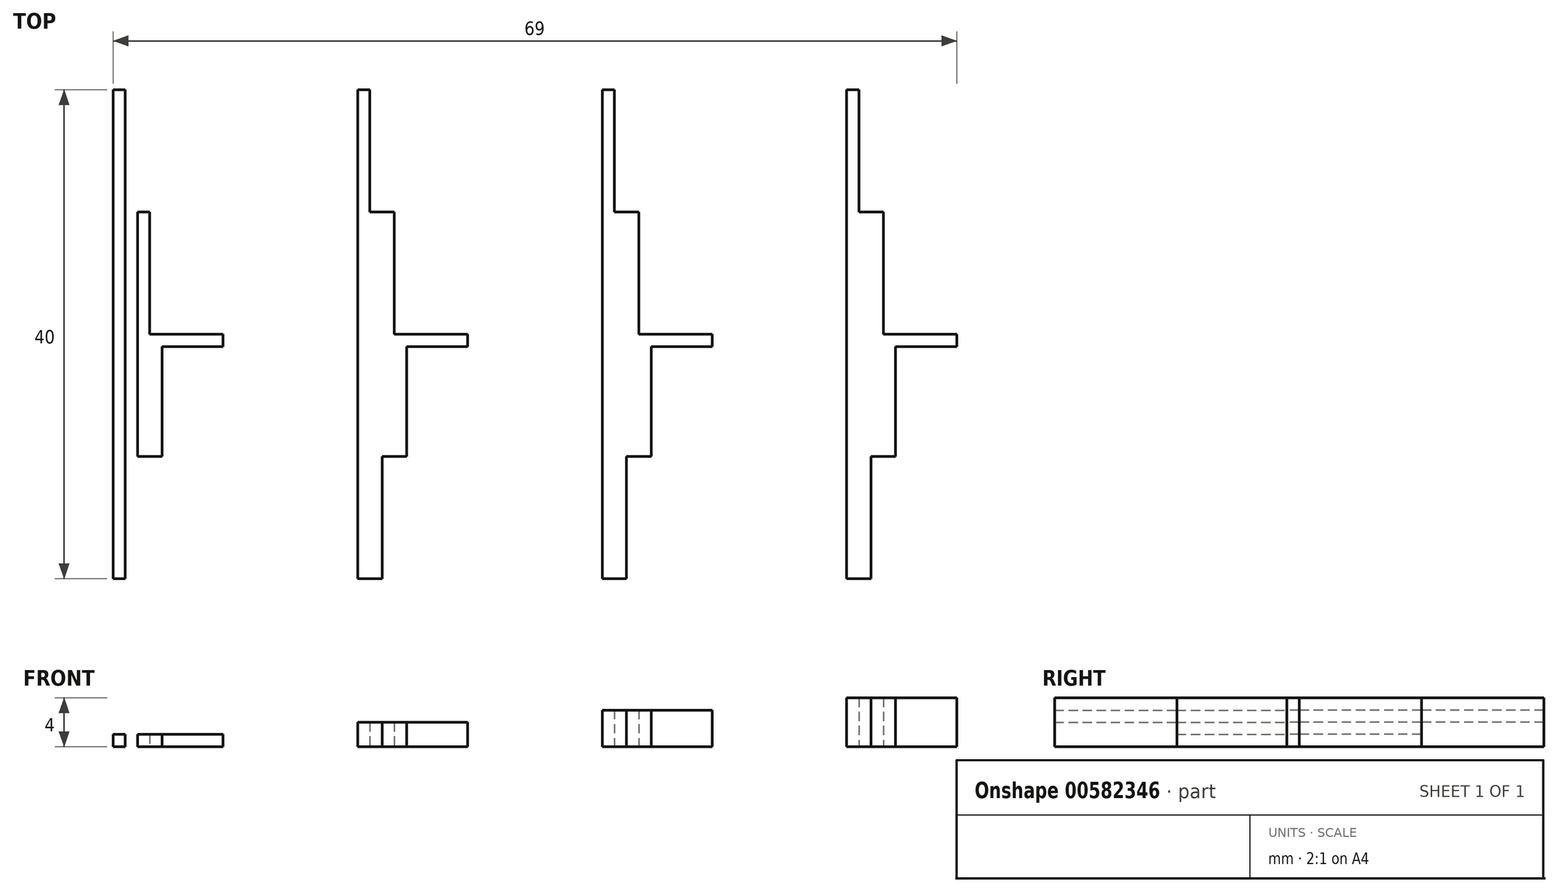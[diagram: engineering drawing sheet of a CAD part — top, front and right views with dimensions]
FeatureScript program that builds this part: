
annotation { "Feature Type Name" : "Feature", "Feature Type Description" : "" }
export const myFeature = defineFeature(function(context is Context, id is Id, definition is map)
    precondition{}
    {
        {
            var Q0;
            Q0=qCreatedBy(makeId("Top.planeOp"),FACE);
            var sketch = newSketch(context, id + "F0", { "sketchPlane" : qUnion([Q0])});
            skLineSegment(sketch, "E0.bottom", {"start": v(-46.97, 24.85) * mm, "end": v(-45.97, 24.85) * mm});
            skLineSegment(sketch, "E0.top", {"start": v(-46.97, -15.15) * mm, "end": v(-45.97, -15.15) * mm});
            skLineSegment(sketch, "E0.left", {"start": v(-46.97, 24.85) * mm, "end": v(-46.97, -15.15) * mm});
            skLineSegment(sketch, "E0.right", {"start": v(-45.97, 24.85) * mm, "end": v(-45.97, -15.15) * mm});
            skLineSegment(sketch, "E1.bottom", {"start": v(-46.97, -15.15) * mm, "end": v(-44.97, -15.15) * mm});
            skLineSegment(sketch, "E2.bottom", {"start": v(-44.97, -15.15) * mm, "end": v(-45.97, -15.15) * mm});
            skLineSegment(sketch, "E2.top", {"start": v(-44.97, 14.85) * mm, "end": v(-45.97, 14.85) * mm});
            skLineSegment(sketch, "E2.left", {"start": v(-44.97, -15.15) * mm, "end": v(-44.97, 14.85) * mm});
            skLineSegment(sketch, "E2.right", {"start": v(-45.97, -15.15) * mm, "end": v(-45.97, 14.85) * mm});
            skLineSegment(sketch, "E3.bottom", {"start": v(-44.97, 14.85) * mm, "end": v(-43.97, 14.85) * mm});
            skLineSegment(sketch, "E3.top", {"start": v(-44.97, -5.15) * mm, "end": v(-43.97, -5.15) * mm});
            skLineSegment(sketch, "E3.left", {"start": v(-44.97, 14.85) * mm, "end": v(-44.97, -5.15) * mm});
            skLineSegment(sketch, "E3.right", {"start": v(-43.97, 14.85) * mm, "end": v(-43.97, -5.15) * mm});
            skLineSegment(sketch, "E4.bottom", {"start": v(-43.97, -5.15) * mm, "end": v(-42.97, -5.15) * mm});
            skLineSegment(sketch, "E4.top", {"start": v(-43.97, 4.85) * mm, "end": v(-42.97, 4.85) * mm});
            skLineSegment(sketch, "E4.left", {"start": v(-43.97, -5.15) * mm, "end": v(-43.97, 4.85) * mm});
            skLineSegment(sketch, "E4.right", {"start": v(-42.97, -5.15) * mm, "end": v(-42.97, 4.85) * mm});
            skLineSegment(sketch, "E5.bottom", {"start": v(-42.97, 4.85) * mm, "end": v(-37.97, 4.85) * mm});
            skLineSegment(sketch, "E5.top", {"start": v(-42.97, 3.85) * mm, "end": v(-37.97, 3.85) * mm});
            skLineSegment(sketch, "E5.left", {"start": v(-42.97, 4.85) * mm, "end": v(-42.97, 3.85) * mm});
            skLineSegment(sketch, "E5.right", {"start": v(-37.97, 4.85) * mm, "end": v(-37.97, 3.85) * mm});
            skLineSegment(sketch, "E6.bottom", {"start": v(-37.97, 3.85) * mm, "end": v(-39.98, 3.85) * mm});
            skLineSegment(sketch, "E7.1.0.0", {"start": v(-25.97, 24.85) * mm, "end": v(-25.97, -15.15) * mm});
            skLineSegment(sketch, "E7.1.0.1", {"start": v(-26.97, 24.85) * mm, "end": v(-26.97, -15.15) * mm});
            skLineSegment(sketch, "E7.1.0.2", {"start": v(-23.97, 14.85) * mm, "end": v(-23.97, -5.15) * mm});
            skLineSegment(sketch, "E7.1.0.3", {"start": v(-24.97, -15.15) * mm, "end": v(-24.97, 14.85) * mm});
            skLineSegment(sketch, "E7.1.0.4", {"start": v(-25.97, -15.15) * mm, "end": v(-25.97, 14.85) * mm});
            skLineSegment(sketch, "E7.1.0.5", {"start": v(-24.97, 14.85) * mm, "end": v(-24.97, -5.15) * mm});
            skLineSegment(sketch, "E7.1.0.6", {"start": v(-22.97, -5.15) * mm, "end": v(-22.97, 4.85) * mm});
            skLineSegment(sketch, "E7.1.0.7", {"start": v(-17.97, 3.85) * mm, "end": v(-19.98, 3.85) * mm});
            skLineSegment(sketch, "E7.1.0.8", {"start": v(-22.97, 4.85) * mm, "end": v(-17.97, 4.85) * mm});
            skLineSegment(sketch, "E7.1.0.9", {"start": v(-23.97, -5.15) * mm, "end": v(-23.97, 4.85) * mm});
            skLineSegment(sketch, "E7.1.0.10", {"start": v(-22.97, 3.85) * mm, "end": v(-17.97, 3.85) * mm});
            skLineSegment(sketch, "E7.1.0.11", {"start": v(-26.97, 24.85) * mm, "end": v(-25.97, 24.85) * mm});
            skLineSegment(sketch, "E7.1.0.12", {"start": v(-17.97, 4.85) * mm, "end": v(-17.97, 3.85) * mm});
            skLineSegment(sketch, "E7.1.0.13", {"start": v(-24.97, -15.15) * mm, "end": v(-25.97, -15.15) * mm});
            skLineSegment(sketch, "E7.1.0.14", {"start": v(-24.97, 14.85) * mm, "end": v(-25.97, 14.85) * mm});
            skLineSegment(sketch, "E7.1.0.15", {"start": v(-26.97, -15.15) * mm, "end": v(-24.97, -15.15) * mm});
            skLineSegment(sketch, "E7.1.0.16", {"start": v(-23.97, 4.85) * mm, "end": v(-22.97, 4.85) * mm});
            skLineSegment(sketch, "E7.1.0.17", {"start": v(-24.97, 14.85) * mm, "end": v(-23.97, 14.85) * mm});
            skLineSegment(sketch, "E7.1.0.18", {"start": v(-22.97, 4.85) * mm, "end": v(-22.97, 3.85) * mm});
            skLineSegment(sketch, "E7.1.0.19", {"start": v(-24.97, -5.15) * mm, "end": v(-23.97, -5.15) * mm});
            skLineSegment(sketch, "E7.1.0.20", {"start": v(-23.97, -5.15) * mm, "end": v(-22.97, -5.15) * mm});
            skLineSegment(sketch, "E7.1.0.21", {"start": v(-26.97, -15.15) * mm, "end": v(-25.97, -15.15) * mm});
            skLineSegment(sketch, "E7.2.0.0", {"start": v(-5.97, 24.85) * mm, "end": v(-5.97, -15.15) * mm});
            skLineSegment(sketch, "E7.2.0.1", {"start": v(-6.97, 24.85) * mm, "end": v(-6.97, -15.15) * mm});
            skLineSegment(sketch, "E7.2.0.2", {"start": v(-3.97, 14.85) * mm, "end": v(-3.97, -5.15) * mm});
            skLineSegment(sketch, "E7.2.0.3", {"start": v(-4.97, -15.15) * mm, "end": v(-4.97, 14.85) * mm});
            skLineSegment(sketch, "E7.2.0.4", {"start": v(-5.97, -15.15) * mm, "end": v(-5.97, 14.85) * mm});
            skLineSegment(sketch, "E7.2.0.5", {"start": v(-4.97, 14.85) * mm, "end": v(-4.97, -5.15) * mm});
            skLineSegment(sketch, "E7.2.0.6", {"start": v(-2.97, -5.15) * mm, "end": v(-2.97, 4.85) * mm});
            skLineSegment(sketch, "E7.2.0.7", {"start": v(2.03, 3.85) * mm, "end": v(0.02, 3.85) * mm});
            skLineSegment(sketch, "E7.2.0.8", {"start": v(-2.97, 4.85) * mm, "end": v(2.03, 4.85) * mm});
            skLineSegment(sketch, "E7.2.0.9", {"start": v(-3.97, -5.15) * mm, "end": v(-3.97, 4.85) * mm});
            skLineSegment(sketch, "E7.2.0.10", {"start": v(-2.97, 3.85) * mm, "end": v(2.03, 3.85) * mm});
            skLineSegment(sketch, "E7.2.0.11", {"start": v(-6.97, 24.85) * mm, "end": v(-5.97, 24.85) * mm});
            skLineSegment(sketch, "E7.2.0.12", {"start": v(2.03, 4.85) * mm, "end": v(2.03, 3.85) * mm});
            skLineSegment(sketch, "E7.2.0.13", {"start": v(-4.97, -15.15) * mm, "end": v(-5.97, -15.15) * mm});
            skLineSegment(sketch, "E7.2.0.14", {"start": v(-4.97, 14.85) * mm, "end": v(-5.97, 14.85) * mm});
            skLineSegment(sketch, "E7.2.0.15", {"start": v(-6.97, -15.15) * mm, "end": v(-4.97, -15.15) * mm});
            skLineSegment(sketch, "E7.2.0.16", {"start": v(-3.97, 4.85) * mm, "end": v(-2.97, 4.85) * mm});
            skLineSegment(sketch, "E7.2.0.17", {"start": v(-4.97, 14.85) * mm, "end": v(-3.97, 14.85) * mm});
            skLineSegment(sketch, "E7.2.0.18", {"start": v(-2.97, 4.85) * mm, "end": v(-2.97, 3.85) * mm});
            skLineSegment(sketch, "E7.2.0.19", {"start": v(-4.97, -5.15) * mm, "end": v(-3.97, -5.15) * mm});
            skLineSegment(sketch, "E7.2.0.20", {"start": v(-3.97, -5.15) * mm, "end": v(-2.97, -5.15) * mm});
            skLineSegment(sketch, "E7.2.0.21", {"start": v(-6.97, -15.15) * mm, "end": v(-5.97, -15.15) * mm});
            skLineSegment(sketch, "E7.3.0.0", {"start": v(14.03, 24.85) * mm, "end": v(14.03, -15.15) * mm});
            skLineSegment(sketch, "E7.3.0.1", {"start": v(13.03, 24.85) * mm, "end": v(13.03, -15.15) * mm});
            skLineSegment(sketch, "E7.3.0.2", {"start": v(16.03, 14.85) * mm, "end": v(16.03, -5.15) * mm});
            skLineSegment(sketch, "E7.3.0.3", {"start": v(15.03, -15.15) * mm, "end": v(15.03, 14.85) * mm});
            skLineSegment(sketch, "E7.3.0.4", {"start": v(14.03, -15.15) * mm, "end": v(14.03, 14.85) * mm});
            skLineSegment(sketch, "E7.3.0.5", {"start": v(15.03, 14.85) * mm, "end": v(15.03, -5.15) * mm});
            skLineSegment(sketch, "E7.3.0.6", {"start": v(17.03, -5.15) * mm, "end": v(17.03, 4.85) * mm});
            skLineSegment(sketch, "E7.3.0.7", {"start": v(22.03, 3.85) * mm, "end": v(20.02, 3.85) * mm});
            skLineSegment(sketch, "E7.3.0.8", {"start": v(17.03, 4.85) * mm, "end": v(22.03, 4.85) * mm});
            skLineSegment(sketch, "E7.3.0.9", {"start": v(16.03, -5.15) * mm, "end": v(16.03, 4.85) * mm});
            skLineSegment(sketch, "E7.3.0.10", {"start": v(17.03, 3.85) * mm, "end": v(22.03, 3.85) * mm});
            skLineSegment(sketch, "E7.3.0.11", {"start": v(13.03, 24.85) * mm, "end": v(14.03, 24.85) * mm});
            skLineSegment(sketch, "E7.3.0.12", {"start": v(22.03, 4.85) * mm, "end": v(22.03, 3.85) * mm});
            skLineSegment(sketch, "E7.3.0.13", {"start": v(15.03, -15.15) * mm, "end": v(14.03, -15.15) * mm});
            skLineSegment(sketch, "E7.3.0.14", {"start": v(15.03, 14.85) * mm, "end": v(14.03, 14.85) * mm});
            skLineSegment(sketch, "E7.3.0.15", {"start": v(13.03, -15.15) * mm, "end": v(15.03, -15.15) * mm});
            skLineSegment(sketch, "E7.3.0.16", {"start": v(16.03, 4.85) * mm, "end": v(17.03, 4.85) * mm});
            skLineSegment(sketch, "E7.3.0.17", {"start": v(15.03, 14.85) * mm, "end": v(16.03, 14.85) * mm});
            skLineSegment(sketch, "E7.3.0.18", {"start": v(17.03, 4.85) * mm, "end": v(17.03, 3.85) * mm});
            skLineSegment(sketch, "E7.3.0.19", {"start": v(15.03, -5.15) * mm, "end": v(16.03, -5.15) * mm});
            skLineSegment(sketch, "E7.3.0.20", {"start": v(16.03, -5.15) * mm, "end": v(17.03, -5.15) * mm});
            skLineSegment(sketch, "E7.3.0.21", {"start": v(13.03, -15.15) * mm, "end": v(14.03, -15.15) * mm});
            skLineSegment(sketch, "E7.direction1", {"start": v(-46.97, -15.15) * mm, "end": v(-26.97, -15.15) * mm, "construction": true});
            skSolve(sketch);
        }
        {
            var Q0;
            Q0=makeQuery(id+"F0.imprint","IMPRINT",FACE,{"disambiguationData":[TD([[makeQuery(id+"F0.imprint","IMPRINT",EDGE,{"derivedFrom":sQuery(id+"F0.wireOp",EDGE,"E0.bottom")}),-1.0]])]});
            var Q1;
            Q1=makeQuery(id+"F0.imprint","IMPRINT",FACE,{"disambiguationData":[TD([[makeQuery(id+"F0.imprint","IMPRINT",EDGE,{"derivedFrom":sQuery(id+"F0.wireOp",EDGE,"E2.bottom")}),-1.0]])]});
            var Q2;
            Q2=makeQuery(id+"F0.imprint","IMPRINT",FACE,{"disambiguationData":[TD([[makeQuery(id+"F0.imprint","IMPRINT",EDGE,{"derivedFrom":sQuery(id+"F0.wireOp",EDGE,"E3.bottom")}),-1.0]])]});
            var Q3;
            Q3=makeQuery(id+"F0.imprint","IMPRINT",FACE,{"disambiguationData":[TD([[makeQuery(id+"F0.imprint","IMPRINT",EDGE,{"derivedFrom":sQuery(id+"F0.wireOp",EDGE,"E4.bottom")}),1.0]])]});
            var Q4;
            Q4=makeQuery(id+"F0.imprint","IMPRINT",FACE,{"disambiguationData":[TD([[makeQuery(id+"F0.imprint","IMPRINT",EDGE,{"derivedFrom":sQuery(id+"F0.wireOp",EDGE,"E5.bottom")}),-1.0]])]});
            extrude(context, id + "F1", {"entities" : qUnion([Q0, Q1, Q2, Q3, Q4]), "depth" : 1 * mm, "offsetDistance" : 25 * mm});
        }
        {
            var Q0;
            Q0=makeQuery(id+"F0.imprint","IMPRINT",FACE,{"disambiguationData":[TD([[makeQuery(id+"F0.imprint","IMPRINT",EDGE,{"derivedFrom":sQuery(id+"F0.wireOp",EDGE,"E7.1.0.0")}),-1.0]])]});
            var Q1;
            Q1=makeQuery(id+"F0.imprint","IMPRINT",FACE,{"disambiguationData":[TD([[makeQuery(id+"F0.imprint","IMPRINT",EDGE,{"derivedFrom":sQuery(id+"F0.wireOp",EDGE,"E7.1.0.3")}),1.0]])]});
            var Q2;
            Q2=makeQuery(id+"F0.imprint","IMPRINT",FACE,{"disambiguationData":[TD([[makeQuery(id+"F0.imprint","IMPRINT",EDGE,{"derivedFrom":sQuery(id+"F0.wireOp",EDGE,"E7.1.0.2")}),-1.0]])]});
            var Q3;
            Q3=makeQuery(id+"F0.imprint","IMPRINT",FACE,{"disambiguationData":[TD([[makeQuery(id+"F0.imprint","IMPRINT",EDGE,{"derivedFrom":sQuery(id+"F0.wireOp",EDGE,"E7.1.0.6")}),1.0]])]});
            var Q4;
            Q4=makeQuery(id+"F0.imprint","IMPRINT",FACE,{"disambiguationData":[TD([[makeQuery(id+"F0.imprint","IMPRINT",EDGE,{"derivedFrom":sQuery(id+"F0.wireOp",EDGE,"E7.1.0.8")}),-1.0]])]});
            extrude(context, id + "F2", {"entities" : qUnion([Q0, Q1, Q2, Q3, Q4]), "depth" : 2 * mm, "offsetDistance" : 25 * mm});
        }
        {
            var Q0;
            Q0=makeQuery(id+"F0.imprint","IMPRINT",FACE,{"disambiguationData":[TD([[makeQuery(id+"F0.imprint","IMPRINT",EDGE,{"derivedFrom":sQuery(id+"F0.wireOp",EDGE,"E7.2.0.0")}),-1.0]])]});
            var Q1;
            Q1=makeQuery(id+"F0.imprint","IMPRINT",FACE,{"disambiguationData":[TD([[makeQuery(id+"F0.imprint","IMPRINT",EDGE,{"derivedFrom":sQuery(id+"F0.wireOp",EDGE,"E7.2.0.2")}),-1.0]])]});
            var Q2;
            Q2=makeQuery(id+"F0.imprint","IMPRINT",FACE,{"disambiguationData":[TD([[makeQuery(id+"F0.imprint","IMPRINT",EDGE,{"derivedFrom":sQuery(id+"F0.wireOp",EDGE,"E7.2.0.6")}),1.0]])]});
            var Q3;
            Q3=makeQuery(id+"F0.imprint","IMPRINT",FACE,{"disambiguationData":[TD([[makeQuery(id+"F0.imprint","IMPRINT",EDGE,{"derivedFrom":sQuery(id+"F0.wireOp",EDGE,"E7.2.0.3")}),1.0]])]});
            var Q4;
            Q4=makeQuery(id+"F0.imprint","IMPRINT",FACE,{"disambiguationData":[TD([[makeQuery(id+"F0.imprint","IMPRINT",EDGE,{"derivedFrom":sQuery(id+"F0.wireOp",EDGE,"E7.2.0.8")}),-1.0]])]});
            extrude(context, id + "F3", {"entities" : qUnion([Q0, Q1, Q2, Q3, Q4]), "depth" : 3 * mm, "offsetDistance" : 25 * mm});
        }
        {
            var Q0;
            Q0=makeQuery(id+"F0.imprint","IMPRINT",FACE,{"disambiguationData":[TD([[makeQuery(id+"F0.imprint","IMPRINT",EDGE,{"derivedFrom":sQuery(id+"F0.wireOp",EDGE,"E7.3.0.0")}),-1.0]])]});
            var Q1;
            Q1=makeQuery(id+"F0.imprint","IMPRINT",FACE,{"disambiguationData":[TD([[makeQuery(id+"F0.imprint","IMPRINT",EDGE,{"derivedFrom":sQuery(id+"F0.wireOp",EDGE,"E7.3.0.3")}),1.0]])]});
            var Q2;
            Q2=makeQuery(id+"F0.imprint","IMPRINT",FACE,{"disambiguationData":[TD([[makeQuery(id+"F0.imprint","IMPRINT",EDGE,{"derivedFrom":sQuery(id+"F0.wireOp",EDGE,"E7.3.0.2")}),-1.0]])]});
            var Q3;
            Q3=makeQuery(id+"F0.imprint","IMPRINT",FACE,{"disambiguationData":[TD([[makeQuery(id+"F0.imprint","IMPRINT",EDGE,{"derivedFrom":sQuery(id+"F0.wireOp",EDGE,"E7.3.0.6")}),1.0]])]});
            var Q4;
            Q4=makeQuery(id+"F0.imprint","IMPRINT",FACE,{"disambiguationData":[TD([[makeQuery(id+"F0.imprint","IMPRINT",EDGE,{"derivedFrom":sQuery(id+"F0.wireOp",EDGE,"E7.3.0.8")}),-1.0]])]});
            extrude(context, id + "F4", {"entities" : qUnion([Q0, Q1, Q2, Q3, Q4]), "depth" : 4 * mm, "offsetDistance" : 25 * mm});
        }
    });
